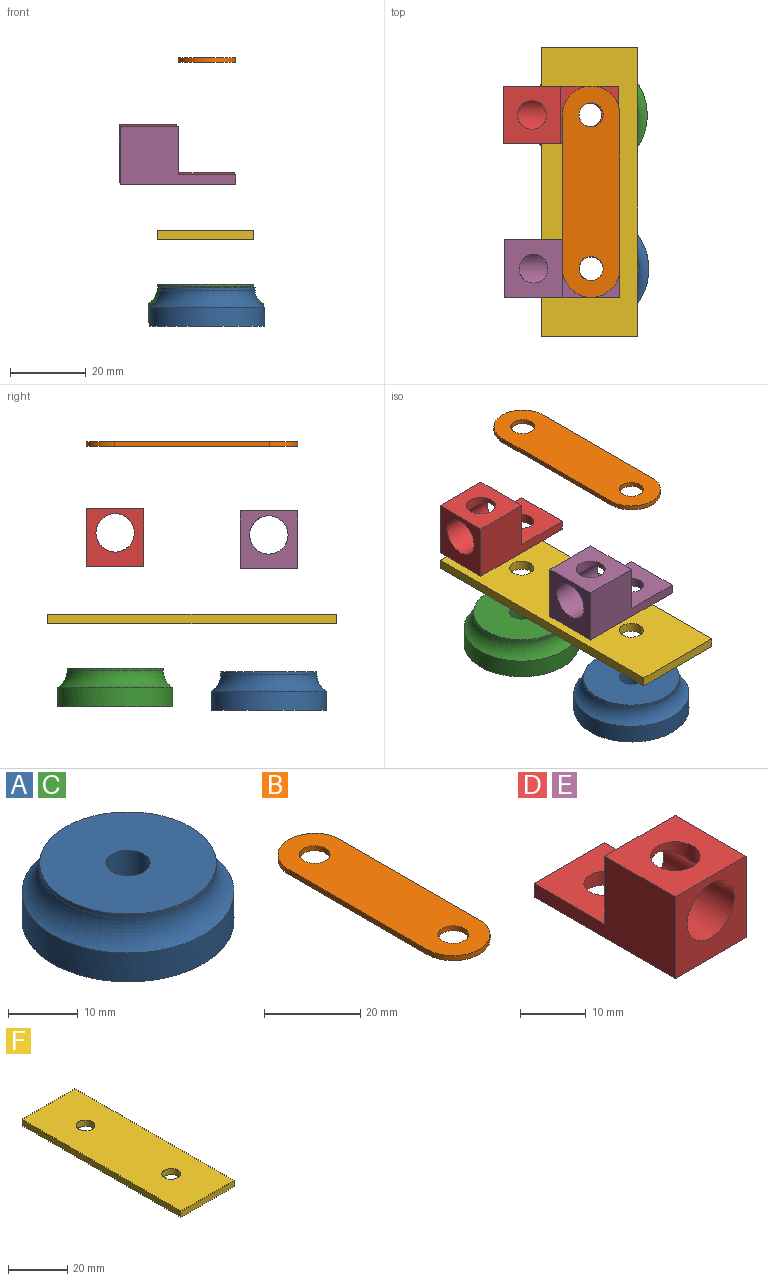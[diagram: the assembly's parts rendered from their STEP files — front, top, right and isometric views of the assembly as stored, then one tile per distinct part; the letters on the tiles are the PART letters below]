
ASSEMBLY  parts=6 mates=4
PART A: 6 faces, bbox 38.5x38.5x13.1 mm
  f0: cylinder r=15.24mm len=30.48mm, axis (0,0,1), area 486.4mm2, adj f1,f5
  f1: plane 30.48x30.48mm, normal (0,0,-1), area 698mm2, adj f0,f4
  f2: cylinder r=12.7mm len=25.4mm, axis (0,0,-1), area 54.3mm2, adj f3,f5
  f3: plane 25.4x25.4mm, normal (0,0,1), area 475mm2, adj f2,f4
  f4: cylinder r=3.17mm len=10.16mm, axis (0,0,1), area 202.7mm2, adj f1,f3
  f5: torus R=17.78mm, axis (0,0,-1), area 453.9mm2, adj f0,f2
PART B: 8 faces, bbox 15.2x55.9x1.3 mm
  f0: cylinder r=7.62mm len=15.16mm, axis (0,0,-1), area 28.8mm2, adj f1,f3,f4,f5
  f1: plane 41.01x1.27mm, normal (-1,0,0), area 52.1mm2, adj f0,f2,f4,f5
  f2: cylinder r=7.62mm len=15.16mm, axis (0,0,-1), area 28.8mm2, adj f1,f3,f4,f5
  f3: plane 42.83x1.27mm, normal (1,0,0), area 54.4mm2, adj f0,f2,f4,f5
  f4: plane 55.88x15.16mm, normal (0,0,1), area 735mm2, adj f0,f1,f2,f3,f6,f7
  f5: plane 55.88x15.16mm, normal (0,0,-1), area 735mm2, adj f0,f1,f2,f3,f6,f7
  f6: cylinder r=3.17mm len=6.35mm, axis (0,0,1), area 25.3mm2, adj f4,f5
  f7: cylinder r=3.17mm len=6.35mm, axis (0,0,1), area 25.3mm2, adj f4,f5
PART C: same geometry as A
PART D: 11 faces, bbox 15.2x30.5x15.2 mm
  f0: plane 15.24x15.24mm, normal (0,0,1), area 200.6mm2, adj f1,f3,f4,f6,f8
  f1: plane 30.48x15.24mm, normal (-1,0,0), area 271mm2, adj f0,f2,f4,f5,f6,f7
  f2: plane 15.24x15.24mm, normal (0,-1,0), area 151.2mm2, adj f1,f3,f5,f7,f9
  f3: plane 30.48x15.24mm, normal (1,0,0), area 271mm2, adj f0,f2,f4,f5,f6,f7
  f4: plane 15.24x2.54mm, normal (0,1,0), area 38.7mm2, adj f0,f1,f3,f5
  f5: plane 30.48x15.24mm, normal (0,0,-1), area 432.8mm2, adj f1,f2,f3,f4,f8
  f6: plane 15.24x12.7mm, normal (0,1,0), area 112.5mm2, adj f0,f1,f3,f7,f9
  f7: plane 15.24x15.24mm, normal (0,0,1), area 186.7mm2, adj f1,f2,f3,f6,f10
  f8: cylinder r=3.17mm len=6.35mm, axis (0,0,1), area 50.7mm2, adj f0,f5
  f9: cylinder r=5.08mm len=15.24mm, axis (0,1,0), area 436.6mm2, adj f2,f6,f10
  f10: cylinder r=3.81mm len=7.62mm, axis (0,0,1), area 49.9mm2, adj f7,f9
PART E: same geometry as D
PART F: 8 faces, bbox 25.4x76.2x2.5 mm
  f0: plane 25.4x2.54mm, normal (0,1,0), area 64.5mm2, adj f1,f3,f4,f5
  f1: plane 76.2x2.54mm, normal (-1,0,0), area 193.5mm2, adj f0,f2,f4,f5
  f2: plane 25.4x2.54mm, normal (0,-1,0), area 64.5mm2, adj f1,f3,f4,f5
  f3: plane 76.2x2.54mm, normal (1,0,0), area 193.5mm2, adj f0,f2,f4,f5
  f4: plane 76.2x25.4mm, normal (0,0,1), area 1872.1mm2, adj f0,f1,f2,f3,f6,f7
  f5: plane 76.2x25.4mm, normal (0,0,-1), area 1872.1mm2, adj f0,f1,f2,f3,f6,f7
  f6: cylinder r=3.17mm len=6.35mm, axis (0,0,1), area 50.7mm2, adj f4,f5
  f7: cylinder r=3.17mm len=6.35mm, axis (0,0,1), area 50.7mm2, adj f4,f5
PLACE A t=(68.11,75.91,24.69)mm fixed
PLACE B t=(68.11,90.67,89.38)mm
PLACE C t=(67.71,116.56,25.67)mm
PLACE D rot(axis=(0,0,-1),90deg) t=(75.33,124.18,57.65)mm
PLACE E rot(axis=(0,0,-1),90deg) t=(75.73,83.53,57.1)mm
PLACE F t=(55.01,58.14,42.48)mm
MATE slider D.f8 <-> F.f7  axis (0,0,1) through (67.71,116.56,60.19)mm
MATE slider E.f8 <-> F.f6  axis (0,0,1) through (68.11,75.91,59.64)mm
MATE slider B.f2 <-> F.f6  axis (0,0,1) through (68.11,75.91,90.02)mm
MATE slider B.f2 <-> A.f0  axis (0,0,1) through (68.11,75.91,90.65)mm
